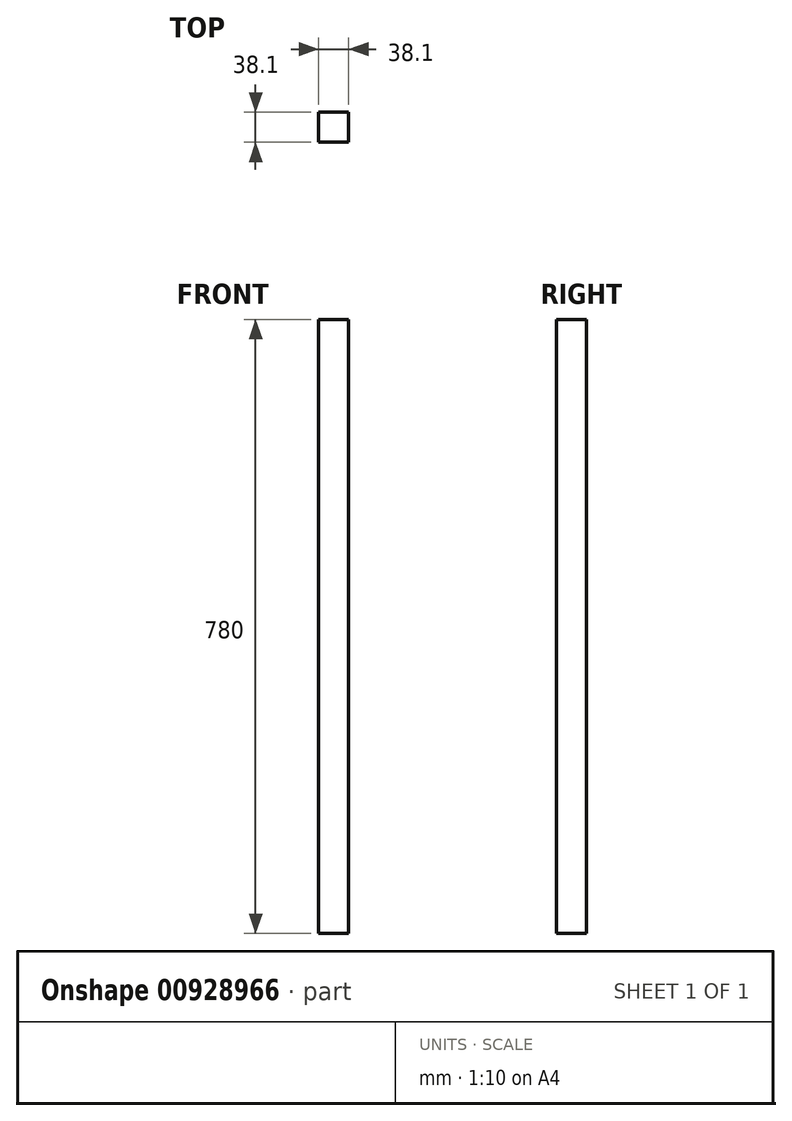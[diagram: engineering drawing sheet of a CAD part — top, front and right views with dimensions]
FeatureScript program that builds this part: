
annotation { "Feature Type Name" : "Feature", "Feature Type Description" : "" }
export const myFeature = defineFeature(function(context is Context, id is Id, definition is map)
    precondition{}
    {
        {
            var Q0;
            Q0=qCreatedBy(makeId("Top.planeOp"),FACE);
            var sketch = newSketch(context, id + "F0", { "sketchPlane" : qUnion([Q0])});
            skLineSegment(sketch, "E0", {"start": v(0, 28.3) * mm, "end": v(0, -25.27) * mm, "construction": true});
            skLineSegment(sketch, "E1", {"start": v(-25.73, 0) * mm, "end": v(27.7, 0) * mm, "construction": true});
            skLineSegment(sketch, "E2.bottom", {"start": v(19.05, -19.05) * mm, "end": v(-19.05, -19.05) * mm});
            skLineSegment(sketch, "E2.top", {"start": v(19.05, 19.05) * mm, "end": v(-19.05, 19.05) * mm});
            skLineSegment(sketch, "E2.left", {"start": v(19.05, -19.05) * mm, "end": v(19.05, 19.05) * mm});
            skLineSegment(sketch, "E2.right", {"start": v(-19.05, -19.05) * mm, "end": v(-19.05, 19.05) * mm});
            skPoint(sketch, "E2.middle", {"position": v(0, 0) * mm});
            skSolve(sketch);
        }
        {
            var Q0;
            Q0 = qSketchRegion(id + "F0", true);
            extrude(context, id + "F1", {"entities" : qUnion([Q0]), "depth" : 780 * mm, "offsetDistance" : 25.4 * mm});
        }
    });
